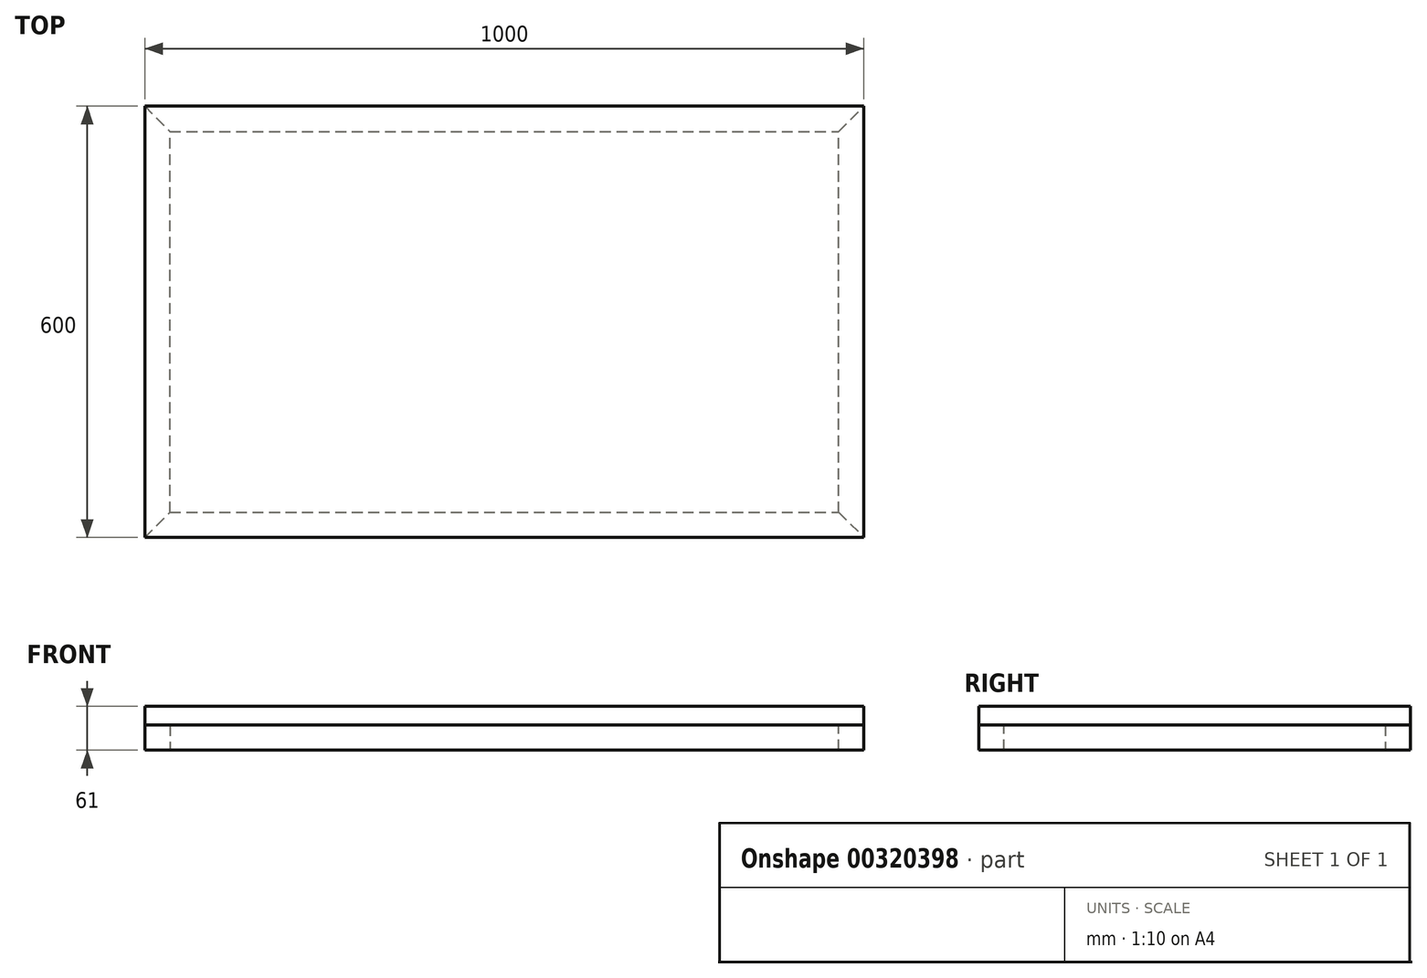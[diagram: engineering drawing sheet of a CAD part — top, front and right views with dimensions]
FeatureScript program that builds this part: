
annotation { "Feature Type Name" : "Feature", "Feature Type Description" : "" }
export const myFeature = defineFeature(function(context is Context, id is Id, definition is map)
    precondition{}
    {
        {
            assignVariable(context, id + "F0", {"name" : "Profilbreite", "anyValue" : 35});
        }
        {
            assignVariable(context, id + "F1", {"name" : "Plattenstaerke", "anyValue" : 26});
        }
        {
            var Q0;
            Q0=qCreatedBy(makeId("Top.planeOp"),FACE);
            var sketch = newSketch(context, id + "F2", { "sketchPlane" : qUnion([Q0])});
            skLineSegment(sketch, "E0.bottom", {"start": v(0, 0) * mm, "end": v(1000, 0) * mm});
            skLineSegment(sketch, "E0.top", {"start": v(0, 600) * mm, "end": v(1000, 600) * mm});
            skLineSegment(sketch, "E0.left", {"start": v(0, 0) * mm, "end": v(0, 600) * mm});
            skLineSegment(sketch, "E0.right", {"start": v(1000, 0) * mm, "end": v(1000, 600) * mm});
            skSolve(sketch);
        }
        {
            var Q0;
            Q0=qCreatedBy(makeId("Top.planeOp"),FACE);
            var sketch = newSketch(context, id + "F3", { "sketchPlane" : qUnion([Q0])});
            skLineSegment(sketch, "E1.bottom", {"start": v(0, 0) * mm, "end": v(1000, 0) * mm});
            skLineSegment(sketch, "E1.top", {"start": v(0, 35) * mm, "end": v(1000, 35) * mm});
            skLineSegment(sketch, "E1.left", {"start": v(0, 0) * mm, "end": v(0, 35) * mm});
            skLineSegment(sketch, "E1.right", {"start": v(1000, 0) * mm, "end": v(1000, 35) * mm});
            skSolve(sketch);
        }
        {
            var Q0;
            Q0=qCreatedBy(makeId("Top.planeOp"),FACE);
            var sketch = newSketch(context, id + "F4", { "sketchPlane" : qUnion([Q0])});
            skLineSegment(sketch, "E2.bottom", {"start": v(0, 0) * mm, "end": v(35, 0) * mm});
            skLineSegment(sketch, "E2.top", {"start": v(0, 600) * mm, "end": v(35, 600) * mm});
            skLineSegment(sketch, "E2.left", {"start": v(0, 0) * mm, "end": v(0, 600) * mm});
            skLineSegment(sketch, "E2.right", {"start": v(35, 0) * mm, "end": v(35, 600) * mm});
            skSolve(sketch);
        }
        {
            var Q0;
            Q0=qCreatedBy(makeId("Top.planeOp"),FACE);
            var sketch = newSketch(context, id + "F5", { "sketchPlane" : qUnion([Q0])});
            skLineSegment(sketch, "E3.bottom", {"start": v(1000, 0) * mm, "end": v(965, 0) * mm});
            skLineSegment(sketch, "E3.top", {"start": v(1000, 600) * mm, "end": v(965, 600) * mm});
            skLineSegment(sketch, "E3.left", {"start": v(1000, 0) * mm, "end": v(1000, 600) * mm});
            skLineSegment(sketch, "E3.right", {"start": v(965, 0) * mm, "end": v(965, 600) * mm});
            skSolve(sketch);
        }
        {
            var Q0;
            Q0=qCreatedBy(makeId("Top.planeOp"),FACE);
            var sketch = newSketch(context, id + "F6", { "sketchPlane" : qUnion([Q0])});
            skLineSegment(sketch, "E4.bottom", {"start": v(0, 600) * mm, "end": v(1000, 600) * mm});
            skLineSegment(sketch, "E4.top", {"start": v(0, 565) * mm, "end": v(1000, 565) * mm});
            skLineSegment(sketch, "E4.left", {"start": v(0, 600) * mm, "end": v(0, 565) * mm});
            skLineSegment(sketch, "E4.right", {"start": v(1000, 600) * mm, "end": v(1000, 565) * mm});
            skSolve(sketch);
        }
        {
            var Q0;
            Q0 = qSketchRegion(id + "F3", true);
            extrude(context, id + "F7", {"entities" : qUnion([Q0]), "depth" : (-(getVariable(context, 'Profilbreite'))) * mm});
        }
        {
            var Q0;
            Q0 = qSketchRegion(id + "F6", true);
            extrude(context, id + "F8", {"entities" : qUnion([Q0]), "depth" : (-(getVariable(context, 'Profilbreite'))) * mm});
        }
        {
            var Q0;
            Q0=makeQuery(id+"F4.imprint","IMPRINT",FACE,{"disambiguationData":[TD([[makeQuery(id+"F4.imprint","IMPRINT",EDGE,{"derivedFrom":sQuery(id+"F4.wireOp",EDGE,"E2.bottom")}),1.0]])]});
            extrude(context, id + "F9", {"entities" : qUnion([Q0]), "depth" : (-(getVariable(context, 'Profilbreite'))) * mm});
        }
        {
            var Q0;
            Q0=makeQuery(id+"F5.imprint","IMPRINT",FACE,{"disambiguationData":[TD([[makeQuery(id+"F5.imprint","IMPRINT",EDGE,{"derivedFrom":sQuery(id+"F5.wireOp",EDGE,"E3.bottom")}),-1.0]])]});
            extrude(context, id + "F10", {"entities" : qUnion([Q0]), "depth" : (-(getVariable(context, 'Profilbreite'))) * mm});
        }
        {
            var Q0;
            Q0=makeQuery(id+"F10.opExtrude","SWEPT_EDGE",EDGE,{"disambiguationData":[OSD([sQuery(id+"F5.wireOp",EDGE,"E3.top"),sQuery(id+"F5.wireOp",EDGE,"E3.right")])]});
            chamfer(context, id + "F11", {"entities" : qUnion([Q0]), "width" : (getVariable(context, 'Profilbreite')) * mm, "tangentPropagation" : true});
        }
        {
            var Q0;
            Q0=makeQuery(id+"F8.opExtrude","SWEPT_EDGE",EDGE,{"disambiguationData":[OSD([sQuery(id+"F6.wireOp",EDGE,"E4.top"),sQuery(id+"F6.wireOp",EDGE,"E4.right")])]});
            chamfer(context, id + "F12", {"entities" : qUnion([Q0]), "width" : (getVariable(context, 'Profilbreite')) * mm, "tangentPropagation" : true});
        }
        {
            var Q0;
            Q0=makeQuery(id+"F10.opExtrude","SWEPT_EDGE",EDGE,{"disambiguationData":[OSD([sQuery(id+"F5.wireOp",EDGE,"E3.bottom"),sQuery(id+"F5.wireOp",EDGE,"E3.right")])]});
            chamfer(context, id + "F13", {"entities" : qUnion([Q0]), "width" : (getVariable(context, 'Profilbreite')) * mm, "tangentPropagation" : true});
        }
        {
            var Q0;
            Q0=makeQuery(id+"F7.opExtrude","SWEPT_EDGE",EDGE,{"disambiguationData":[OSD([sQuery(id+"F3.wireOp",EDGE,"E1.top"),sQuery(id+"F3.wireOp",EDGE,"E1.right")])]});
            chamfer(context, id + "F14", {"entities" : qUnion([Q0]), "width" : (getVariable(context, 'Profilbreite')) * mm, "tangentPropagation" : true});
        }
        {
            var Q0;
            Q0=makeQuery(id+"F7.opExtrude","SWEPT_EDGE",EDGE,{"disambiguationData":[OSD([sQuery(id+"F3.wireOp",EDGE,"E1.top"),sQuery(id+"F3.wireOp",EDGE,"E1.left")])]});
            var Q1;
            Q1=makeQuery(id+"F9.opExtrude","SWEPT_EDGE",EDGE,{"disambiguationData":[OSD([sQuery(id+"F4.wireOp",EDGE,"E2.bottom"),sQuery(id+"F4.wireOp",EDGE,"E2.right")])]});
            chamfer(context, id + "F15", {"entities" : qUnion([Q0, Q1]), "width" : (getVariable(context, 'Profilbreite')) * mm, "tangentPropagation" : true});
        }
        {
            var Q0;
            Q0=makeQuery(id+"F9.opExtrude","SWEPT_EDGE",EDGE,{"disambiguationData":[OSD([sQuery(id+"F4.wireOp",EDGE,"E2.top"),sQuery(id+"F4.wireOp",EDGE,"E2.right")])]});
            var Q1;
            Q1=makeQuery(id+"F8.opExtrude","SWEPT_EDGE",EDGE,{"disambiguationData":[OSD([sQuery(id+"F6.wireOp",EDGE,"E4.top"),sQuery(id+"F6.wireOp",EDGE,"E4.left")])]});
            chamfer(context, id + "F16", {"entities" : qUnion([Q0, Q1]), "width" : (getVariable(context, 'Profilbreite')) * mm, "tangentPropagation" : true});
        }
        {
            var Q0;
            Q0 = qSketchRegion(id + "F2", true);
            extrude(context, id + "F17", {"entities" : qUnion([Q0]), "depth" : (getVariable(context, 'Plattenstaerke')) * mm});
        }
    });
